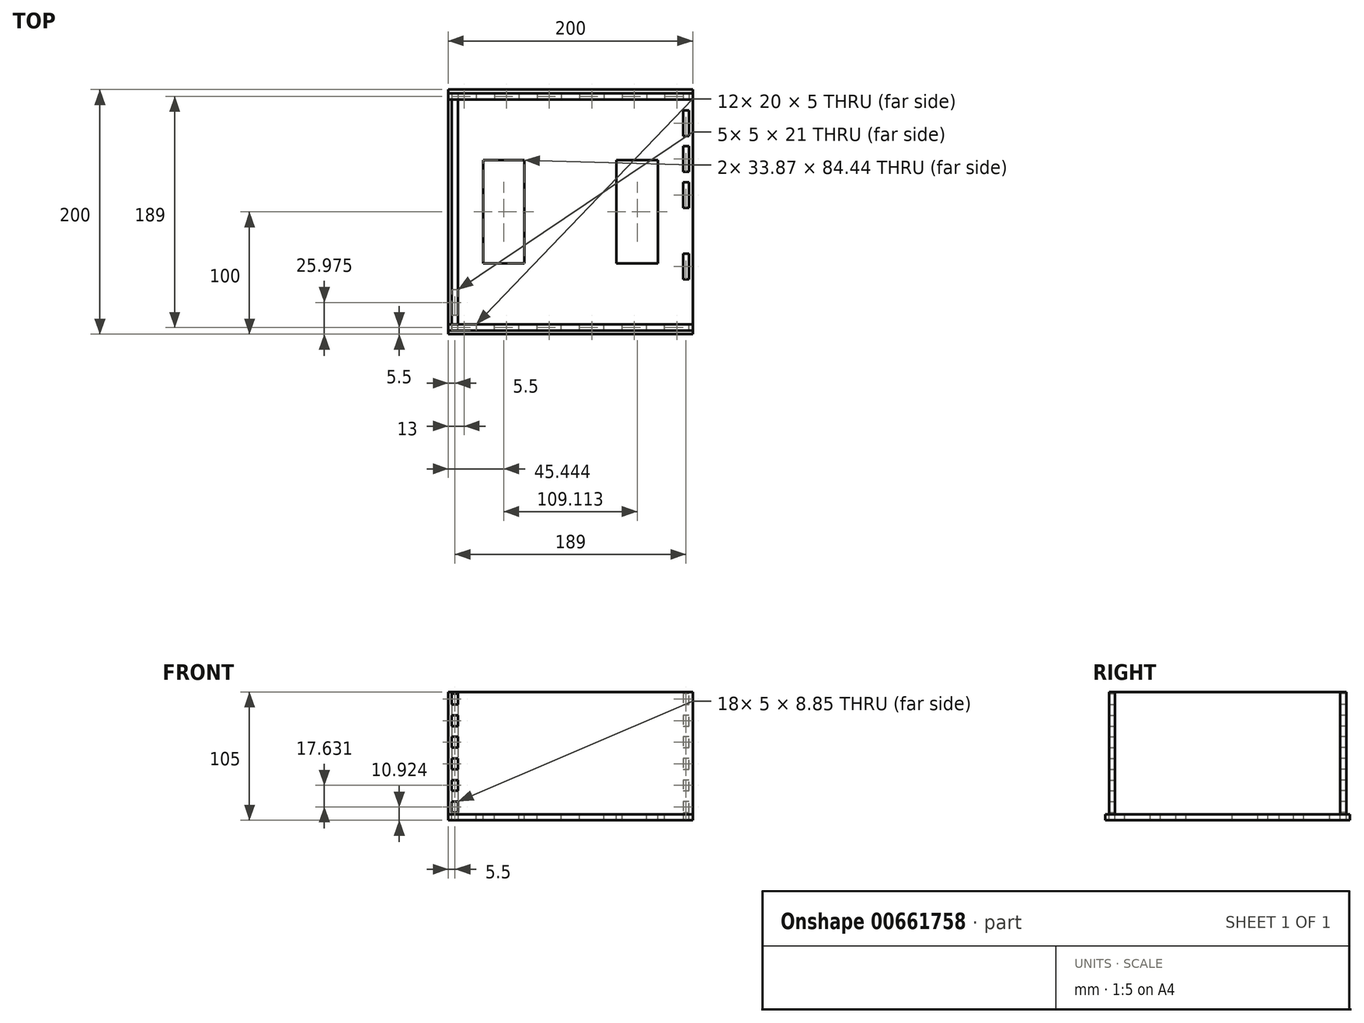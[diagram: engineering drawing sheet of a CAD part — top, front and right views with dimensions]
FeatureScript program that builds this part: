
annotation { "Feature Type Name" : "Feature", "Feature Type Description" : "" }
export const myFeature = defineFeature(function(context is Context, id is Id, definition is map)
    precondition{}
    {
        {
            assignVariable(context, id + "F0", {"name" : "width", "anyValue" : 5});
        }
        {
            var Q0;
            Q0=qCreatedBy(makeId("Top.planeOp"),FACE);
            var sketch = newSketch(context, id + "F1", { "sketchPlane" : qUnion([Q0])});
            skLineSegment(sketch, "E0.bottom", {"start": v(100, -100) * mm, "end": v(-100, -100) * mm});
            skLineSegment(sketch, "E0.top", {"start": v(100, 100) * mm, "end": v(-100, 100) * mm});
            skLineSegment(sketch, "E0.left", {"start": v(100, -100) * mm, "end": v(100, 100) * mm});
            skLineSegment(sketch, "E0.right", {"start": v(-100, -100) * mm, "end": v(-100, 100) * mm});
            skPoint(sketch, "E0.middle", {"position": v(0, 0) * mm});
            skLineSegment(sketch, "E1.0", {"start": v(97, 97) * mm, "end": v(-97, 97) * mm, "construction": true});
            skLineSegment(sketch, "E1.1", {"start": v(97, -97) * mm, "end": v(97, 97) * mm, "construction": true});
            skLineSegment(sketch, "E1.2", {"start": v(97, -97) * mm, "end": v(-97, -97) * mm, "construction": true});
            skLineSegment(sketch, "E1.3", {"start": v(-97, -97) * mm, "end": v(-97, 97) * mm, "construction": true});
            skSolve(sketch);
        }
        {
            var Q0;
            Q0=qSketchRegion(id+"F1",true);
            extrude(context, id + "F2", {"entities" : qUnion([Q0]), "depth" : (getVariable(context, 'width')) * mm});
        }
        {
            var Q0;
            Q0=makeQuery(id+"F2.opExtrude","CAP_FACE",FACE,{"disambiguationData":[OSD([sQuery(id+"F1.wireOp",EDGE,"E0.bottom"),sQuery(id+"F1.wireOp",EDGE,"E0.top"),sQuery(id+"F1.wireOp",EDGE,"E0.left"),sQuery(id+"F1.wireOp",EDGE,"E0.right")])],"isStart":false});
            var sketch = newSketch(context, id + "F3", { "sketchPlane" : qUnion([Q0])});
            skLineSegment(sketch, "E2.0", {"start": v(97, 97) * mm, "end": v(-97, 97) * mm, "construction": true});
            skLineSegment(sketch, "E2.1", {"start": v(97, -97) * mm, "end": v(97, 97) * mm, "construction": true});
            skLineSegment(sketch, "E2.2", {"start": v(97, -97) * mm, "end": v(-97, -97) * mm, "construction": true});
            skLineSegment(sketch, "E2.3", {"start": v(-97, -97) * mm, "end": v(-97, 97) * mm, "construction": true});
            skLineSegment(sketch, "E3.bottom", {"start": v(-97, 97) * mm, "end": v(-77, 97) * mm, "construction": true});
            skLineSegment(sketch, "E3.left", {"start": v(-97, 97) * mm, "end": v(-97, 92) * mm, "construction": true});
            skLineSegment(sketch, "E4.bottom", {"start": v(-97, 97) * mm, "end": v(-77, 97) * mm});
            skLineSegment(sketch, "E4.top", {"start": v(-97, 92) * mm, "end": v(-77, 92) * mm});
            skLineSegment(sketch, "E4.left", {"start": v(-97, 97) * mm, "end": v(-97, 92) * mm});
            skLineSegment(sketch, "E4.right", {"start": v(-77, 97) * mm, "end": v(-77, 92) * mm});
            skLineSegment(sketch, "E5.1.0.0", {"start": v(-42.2, 97) * mm, "end": v(-42.2, 92) * mm});
            skLineSegment(sketch, "E5.1.0.1", {"start": v(-62.2, 92) * mm, "end": v(-42.2, 92) * mm});
            skLineSegment(sketch, "E5.1.0.2", {"start": v(-62.2, 97) * mm, "end": v(-42.2, 97) * mm});
            skLineSegment(sketch, "E5.1.0.3", {"start": v(-62.2, 97) * mm, "end": v(-62.2, 92) * mm});
            skLineSegment(sketch, "E5.2.0.0", {"start": v(-7.4, 97) * mm, "end": v(-7.4, 92) * mm});
            skLineSegment(sketch, "E5.2.0.1", {"start": v(-27.4, 92) * mm, "end": v(-7.4, 92) * mm});
            skLineSegment(sketch, "E5.2.0.2", {"start": v(-27.4, 97) * mm, "end": v(-7.4, 97) * mm});
            skLineSegment(sketch, "E5.2.0.3", {"start": v(-27.4, 97) * mm, "end": v(-27.4, 92) * mm});
            skLineSegment(sketch, "E5.3.0.0", {"start": v(27.4, 97) * mm, "end": v(27.4, 92) * mm});
            skLineSegment(sketch, "E5.3.0.1", {"start": v(7.4, 92) * mm, "end": v(27.4, 92) * mm});
            skLineSegment(sketch, "E5.3.0.2", {"start": v(7.4, 97) * mm, "end": v(27.4, 97) * mm});
            skLineSegment(sketch, "E5.3.0.3", {"start": v(7.4, 97) * mm, "end": v(7.4, 92) * mm});
            skLineSegment(sketch, "E5.4.0.0", {"start": v(62.2, 97) * mm, "end": v(62.2, 92) * mm});
            skLineSegment(sketch, "E5.4.0.1", {"start": v(42.2, 92) * mm, "end": v(62.2, 92) * mm});
            skLineSegment(sketch, "E5.4.0.2", {"start": v(42.2, 97) * mm, "end": v(62.2, 97) * mm});
            skLineSegment(sketch, "E5.4.0.3", {"start": v(42.2, 97) * mm, "end": v(42.2, 92) * mm});
            skLineSegment(sketch, "E5.5.0.0", {"start": v(97, 97) * mm, "end": v(97, 92) * mm});
            skLineSegment(sketch, "E5.5.0.1", {"start": v(77, 92) * mm, "end": v(97, 92) * mm});
            skLineSegment(sketch, "E5.5.0.2", {"start": v(77, 97) * mm, "end": v(97, 97) * mm});
            skLineSegment(sketch, "E5.5.0.3", {"start": v(77, 97) * mm, "end": v(77, 92) * mm});
            skLineSegment(sketch, "E5.direction1", {"start": v(-77, 92) * mm, "end": v(-42.2, 92) * mm, "construction": true});
            skLineSegment(sketch, "E6.MirrorCS", {"start": v(-97, -97) * mm, "end": v(-97, -92) * mm});
            skLineSegment(sketch, "E7.MirrorCS", {"start": v(-77, -97) * mm, "end": v(-77, -92) * mm});
            skLineSegment(sketch, "E8.MirrorCS", {"start": v(-97, -97) * mm, "end": v(-97, -92) * mm, "construction": true});
            skLineSegment(sketch, "E9.MirrorCS", {"start": v(97, -97) * mm, "end": v(97, -92) * mm});
            skLineSegment(sketch, "E10.MirrorCS", {"start": v(77, -97) * mm, "end": v(77, -92) * mm});
            skLineSegment(sketch, "E11.MirrorCS", {"start": v(-42.2, -97) * mm, "end": v(-42.2, -92) * mm});
            skLineSegment(sketch, "E12.MirrorCS", {"start": v(62.2, -97) * mm, "end": v(62.2, -92) * mm});
            skLineSegment(sketch, "E13.MirrorCS", {"start": v(-62.2, -97) * mm, "end": v(-62.2, -92) * mm});
            skLineSegment(sketch, "E14.MirrorCS", {"start": v(-7.4, -97) * mm, "end": v(-7.4, -92) * mm});
            skLineSegment(sketch, "E15.MirrorCS", {"start": v(-27.4, -97) * mm, "end": v(-27.4, -92) * mm});
            skLineSegment(sketch, "E16.MirrorCS", {"start": v(7.4, -97) * mm, "end": v(7.4, -92) * mm});
            skLineSegment(sketch, "E17.MirrorCS", {"start": v(27.4, -97) * mm, "end": v(27.4, -92) * mm});
            skLineSegment(sketch, "E18.MirrorCS", {"start": v(42.2, -97) * mm, "end": v(42.2, -92) * mm});
            skLineSegment(sketch, "E19.MirrorCS", {"start": v(-62.2, -92) * mm, "end": v(-42.2, -92) * mm});
            skLineSegment(sketch, "E20.MirrorCS", {"start": v(-27.4, -97) * mm, "end": v(-7.4, -97) * mm});
            skLineSegment(sketch, "E21.MirrorCS", {"start": v(7.4, -97) * mm, "end": v(27.4, -97) * mm});
            skLineSegment(sketch, "E22.MirrorCS", {"start": v(42.2, -97) * mm, "end": v(62.2, -97) * mm});
            skLineSegment(sketch, "E23.MirrorCS", {"start": v(77, -97) * mm, "end": v(97, -97) * mm});
            skLineSegment(sketch, "E24.MirrorCS", {"start": v(-62.2, -97) * mm, "end": v(-42.2, -97) * mm});
            skLineSegment(sketch, "E25.MirrorCS", {"start": v(-97, -97) * mm, "end": v(-77, -97) * mm});
            skLineSegment(sketch, "E26.MirrorCS", {"start": v(42.2, -92) * mm, "end": v(62.2, -92) * mm});
            skLineSegment(sketch, "E27.MirrorCS", {"start": v(77, -92) * mm, "end": v(97, -92) * mm});
            skLineSegment(sketch, "E28.MirrorCS", {"start": v(-77, -92) * mm, "end": v(-42.2, -92) * mm, "construction": true});
            skLineSegment(sketch, "E29.MirrorCS", {"start": v(-27.4, -92) * mm, "end": v(-7.4, -92) * mm});
            skLineSegment(sketch, "E30.MirrorCS", {"start": v(-97, -97) * mm, "end": v(-77, -97) * mm, "construction": true});
            skLineSegment(sketch, "E31.MirrorCS", {"start": v(-97, -92) * mm, "end": v(-77, -92) * mm});
            skLineSegment(sketch, "E32.MirrorCS", {"start": v(7.4, -92) * mm, "end": v(27.4, -92) * mm});
            skSolve(sketch);
        }
        {
            var Q0;
            Q0=qSketchRegion(id+"F3",true);
            extrude(context, id + "F4", {"entities" : qUnion([Q0]), "operationType" : NewBodyOperationType.REMOVE, "oppositeDirection" : true, "depth" : 25 * mm});
        }
        {
            var Q0;
            Q0=makeQuery(id+"F2.opExtrude","CAP_FACE",FACE,{"disambiguationData":[OSD([sQuery(id+"F1.wireOp",EDGE,"E0.bottom"),sQuery(id+"F1.wireOp",EDGE,"E0.top"),sQuery(id+"F1.wireOp",EDGE,"E0.left"),sQuery(id+"F1.wireOp",EDGE,"E0.right")])],"isStart":false});
            var sketch = newSketch(context, id + "F5", { "sketchPlane" : qUnion([Q0])});
            skLineSegment(sketch, "E33.0", {"start": v(-97, 97) * mm, "end": v(-77, 97) * mm});
            skSolve(sketch);
        }
        {
            var Q0;
            Q0=makeQuery(id+"F5.imprint","IMPRINT",FACE,{"disambiguationData":[TD([[makeQuery(id+"F5.imprint","IMPRINT",EDGE,{"derivedFrom":makeQuery(id+"F4.boolean.opBoolean","COPY",EDGE,{"derivedFrom":makeQuery(id+"F4.opExtrude","CAP_EDGE",EDGE,{"disambiguationData":[OSD([sQuery(id+"F3.wireOp",EDGE,"E5.1.0.0")])],"isStart":true})})}),-1.0]])]});
            var Q1;
            Q1=makeQuery(id+"F5.imprint","IMPRINT",FACE,{"disambiguationData":[TD([[makeQuery(id+"F5.imprint","IMPRINT",EDGE,{"derivedFrom":sQuery(id+"F5.wireOp",EDGE,"E33.0")}),-1.0]])]});
            var Q2;
            Q2=makeQuery(id+"F5.imprint","IMPRINT",FACE,{"disambiguationData":[TD([[makeQuery(id+"F5.imprint","IMPRINT",EDGE,{"derivedFrom":makeQuery(id+"F4.boolean.opBoolean","COPY",EDGE,{"derivedFrom":makeQuery(id+"F4.opExtrude","CAP_EDGE",EDGE,{"disambiguationData":[OSD([sQuery(id+"F3.wireOp",EDGE,"E5.2.0.0")])],"isStart":true})})}),-1.0]])]});
            var Q3;
            Q3=makeQuery(id+"F5.imprint","IMPRINT",FACE,{"disambiguationData":[TD([[makeQuery(id+"F5.imprint","IMPRINT",EDGE,{"derivedFrom":makeQuery(id+"F4.boolean.opBoolean","COPY",EDGE,{"derivedFrom":makeQuery(id+"F4.opExtrude","CAP_EDGE",EDGE,{"disambiguationData":[OSD([sQuery(id+"F3.wireOp",EDGE,"E5.3.0.0")])],"isStart":true})})}),-1.0]])]});
            var Q4;
            Q4=makeQuery(id+"F5.imprint","IMPRINT",FACE,{"disambiguationData":[TD([[makeQuery(id+"F5.imprint","IMPRINT",EDGE,{"derivedFrom":makeQuery(id+"F4.boolean.opBoolean","COPY",EDGE,{"derivedFrom":makeQuery(id+"F4.opExtrude","CAP_EDGE",EDGE,{"disambiguationData":[OSD([sQuery(id+"F3.wireOp",EDGE,"E5.4.0.0")])],"isStart":true})})}),-1.0]])]});
            var Q5;
            Q5=makeQuery(id+"F5.imprint","IMPRINT",FACE,{"disambiguationData":[TD([[makeQuery(id+"F5.imprint","IMPRINT",EDGE,{"derivedFrom":makeQuery(id+"F4.boolean.opBoolean","COPY",EDGE,{"derivedFrom":makeQuery(id+"F4.opExtrude","CAP_EDGE",EDGE,{"disambiguationData":[OSD([sQuery(id+"F3.wireOp",EDGE,"E5.5.0.0")])],"isStart":true})})}),-1.0]])]});
            var Q6;
            Q6=makeQuery(id+"F2.opExtrude","CAP_FACE",FACE,{"disambiguationData":[OSD([sQuery(id+"F1.wireOp",EDGE,"E0.bottom"),sQuery(id+"F1.wireOp",EDGE,"E0.top"),sQuery(id+"F1.wireOp",EDGE,"E0.left"),sQuery(id+"F1.wireOp",EDGE,"E0.right")])],"isStart":true});
            extrude(context, id + "F6", {"entities" : qUnion([Q0, Q1, Q2, Q3, Q4, Q5]), "endBound" : BoundingType.UP_TO_SURFACE, "oppositeDirection" : true, "endBoundEntityFace" : qUnion([Q6]), "depth" : 25 * mm});
        }
        {
            var Q0;
            Q0=makeQuery(id+"F2.opExtrude","CAP_FACE",FACE,{"disambiguationData":[OSD([sQuery(id+"F1.wireOp",EDGE,"E0.bottom"),sQuery(id+"F1.wireOp",EDGE,"E0.top"),sQuery(id+"F1.wireOp",EDGE,"E0.left"),sQuery(id+"F1.wireOp",EDGE,"E0.right")])],"isStart":false});
            var sketch = newSketch(context, id + "F7", { "sketchPlane" : qUnion([Q0])});
            skLineSegment(sketch, "E34.bottom", {"start": v(-100, 97) * mm, "end": v(100, 97) * mm});
            skLineSegment(sketch, "E34.top", {"start": v(-100, 92) * mm, "end": v(100, 92) * mm});
            skLineSegment(sketch, "E34.left", {"start": v(-100, 97) * mm, "end": v(-100, 92) * mm});
            skLineSegment(sketch, "E34.right", {"start": v(100, 97) * mm, "end": v(100, 92) * mm});
            skSolve(sketch);
        }
        {
            var Q0;
            Q0=qSketchRegion(id+"F7",true);
            extrude(context, id + "F8", {"entities" : qUnion([Q0]), "depth" : 100 * mm});
        }
        {
            var Q0;
            Q0=makeQuery(id+"F2.opExtrude","CAP_FACE",FACE,{"disambiguationData":[OSD([sQuery(id+"F1.wireOp",EDGE,"E0.bottom"),sQuery(id+"F1.wireOp",EDGE,"E0.top"),sQuery(id+"F1.wireOp",EDGE,"E0.left"),sQuery(id+"F1.wireOp",EDGE,"E0.right")])],"isStart":true});
            var sketch = newSketch(context, id + "F9", { "sketchPlane" : qUnion([Q0])});
            skLineSegment(sketch, "E35.0", {"start": v(97, 97) * mm, "end": v(97, -97) * mm});
            skLineSegment(sketch, "E35.1", {"start": v(97, 97) * mm, "end": v(-97, 97) * mm});
            skLineSegment(sketch, "E35.2", {"start": v(-97, 97) * mm, "end": v(-97, -97) * mm});
            skLineSegment(sketch, "E35.3", {"start": v(97, -97) * mm, "end": v(-97, -97) * mm});
            skLineSegment(sketch, "E36.bottom", {"start": v(-97, 84.52) * mm, "end": v(-92, 84.52) * mm});
            skLineSegment(sketch, "E36.top", {"start": v(-97, 63.52) * mm, "end": v(-92, 63.52) * mm});
            skLineSegment(sketch, "E36.left", {"start": v(-97, 84.52) * mm, "end": v(-97, 63.52) * mm});
            skLineSegment(sketch, "E36.right", {"start": v(-92, 84.52) * mm, "end": v(-92, 63.52) * mm});
            skLineSegment(sketch, "E37.1.0.0", {"start": v(-97, 55.22) * mm, "end": v(-97, 34.22) * mm});
            skLineSegment(sketch, "E37.1.0.1", {"start": v(-97, 55.22) * mm, "end": v(-92, 55.22) * mm});
            skLineSegment(sketch, "E37.1.0.2", {"start": v(-97, 34.22) * mm, "end": v(-92, 34.22) * mm});
            skLineSegment(sketch, "E37.1.0.3", {"start": v(-92, 55.22) * mm, "end": v(-92, 34.22) * mm});
            skLineSegment(sketch, "E37.2.0.0", {"start": v(-97, 25.91) * mm, "end": v(-97, 4.91) * mm});
            skLineSegment(sketch, "E37.2.0.1", {"start": v(-97, 25.91) * mm, "end": v(-92, 25.91) * mm});
            skLineSegment(sketch, "E37.2.0.2", {"start": v(-97, 4.91) * mm, "end": v(-92, 4.91) * mm});
            skLineSegment(sketch, "E37.2.0.3", {"start": v(-92, 25.91) * mm, "end": v(-92, 4.91) * mm});
            skLineSegment(sketch, "E37.3.0.0", {"start": v(-97, -3.4) * mm, "end": v(-97, -24.4) * mm});
            skLineSegment(sketch, "E37.3.0.1", {"start": v(-97, -3.4) * mm, "end": v(-92, -3.4) * mm});
            skLineSegment(sketch, "E37.3.0.2", {"start": v(-97, -24.4) * mm, "end": v(-92, -24.4) * mm});
            skLineSegment(sketch, "E37.3.0.3", {"start": v(-92, -3.4) * mm, "end": v(-92, -24.4) * mm});
            skLineSegment(sketch, "E37.4.0.0", {"start": v(-97, -32.7) * mm, "end": v(-97, -53.7) * mm});
            skLineSegment(sketch, "E37.4.0.1", {"start": v(-97, -32.7) * mm, "end": v(-92, -32.7) * mm});
            skLineSegment(sketch, "E37.4.0.2", {"start": v(-97, -53.7) * mm, "end": v(-92, -53.7) * mm});
            skLineSegment(sketch, "E37.4.0.3", {"start": v(-92, -32.7) * mm, "end": v(-92, -53.7) * mm});
            skLineSegment(sketch, "E37.5.0.0", {"start": v(-97, -62) * mm, "end": v(-97, -83) * mm});
            skLineSegment(sketch, "E37.5.0.1", {"start": v(-97, -62) * mm, "end": v(-92, -62) * mm});
            skLineSegment(sketch, "E37.5.0.2", {"start": v(-97, -83) * mm, "end": v(-92, -83) * mm});
            skLineSegment(sketch, "E37.5.0.3", {"start": v(-92, -62) * mm, "end": v(-92, -83) * mm});
            skLineSegment(sketch, "E37.direction1", {"start": v(-97, 63.52) * mm, "end": v(-97, 34.22) * mm, "construction": true});
            skLineSegment(sketch, "E38.MirrorCS", {"start": v(97, 84.52) * mm, "end": v(97, 63.52) * mm});
            skLineSegment(sketch, "E39.MirrorCS", {"start": v(97, 84.52) * mm, "end": v(92, 84.52) * mm});
            skLineSegment(sketch, "E40.MirrorCS", {"start": v(92, 84.52) * mm, "end": v(92, 63.52) * mm});
            skLineSegment(sketch, "E41.MirrorCS", {"start": v(97, 63.52) * mm, "end": v(92, 63.52) * mm});
            skLineSegment(sketch, "E42.MirrorCS", {"start": v(97, 55.22) * mm, "end": v(92, 55.22) * mm});
            skLineSegment(sketch, "E43.MirrorCS", {"start": v(92, 55.22) * mm, "end": v(92, 34.22) * mm});
            skLineSegment(sketch, "E44.MirrorCS", {"start": v(97, 63.52) * mm, "end": v(97, 34.22) * mm, "construction": true});
            skLineSegment(sketch, "E45.MirrorCS", {"start": v(97, 55.22) * mm, "end": v(97, 34.22) * mm});
            skLineSegment(sketch, "E46.MirrorCS", {"start": v(97, 25.91) * mm, "end": v(97, 4.91) * mm});
            skLineSegment(sketch, "E47.MirrorCS", {"start": v(97, 34.22) * mm, "end": v(92, 34.22) * mm});
            skLineSegment(sketch, "E48.MirrorCS", {"start": v(97, 25.91) * mm, "end": v(92, 25.91) * mm});
            skLineSegment(sketch, "E49.MirrorCS", {"start": v(92, 25.91) * mm, "end": v(92, 4.91) * mm});
            skLineSegment(sketch, "E50.MirrorCS", {"start": v(97, 4.91) * mm, "end": v(92, 4.91) * mm});
            skLineSegment(sketch, "E51.MirrorCS", {"start": v(97, -32.7) * mm, "end": v(92, -32.7) * mm});
            skLineSegment(sketch, "E52.MirrorCS", {"start": v(92, -32.7) * mm, "end": v(92, -53.7) * mm});
            skLineSegment(sketch, "E53.MirrorCS", {"start": v(97, -32.7) * mm, "end": v(97, -53.7) * mm});
            skLineSegment(sketch, "E54.MirrorCS", {"start": v(97, -53.7) * mm, "end": v(92, -53.7) * mm});
            skLineSegment(sketch, "E55.MirrorCS", {"start": v(97, -62) * mm, "end": v(92, -62) * mm});
            skLineSegment(sketch, "E56.MirrorCS", {"start": v(92, -62) * mm, "end": v(92, -83) * mm});
            skLineSegment(sketch, "E57.MirrorCS", {"start": v(97, -62) * mm, "end": v(97, -83) * mm});
            skLineSegment(sketch, "E58.MirrorCS", {"start": v(97, -83) * mm, "end": v(92, -83) * mm});
            skLineSegment(sketch, "E59.MirrorCS", {"start": v(92, -3.4) * mm, "end": v(92, -24.4) * mm});
            skLineSegment(sketch, "E60.MirrorCS", {"start": v(97, -3.4) * mm, "end": v(92, -3.4) * mm});
            skLineSegment(sketch, "E61.MirrorCS", {"start": v(97, -24.4) * mm, "end": v(92, -24.4) * mm});
            skLineSegment(sketch, "E62.MirrorCS", {"start": v(97, -3.4) * mm, "end": v(97, -24.4) * mm});
            skSolve(sketch);
        }
        {
            var Q0;
            Q0=makeQuery(id+"F9.imprint","IMPRINT",FACE,{"disambiguationData":[TD([[makeQuery(id+"F9.imprint","IMPRINT",EDGE,{"derivedFrom":sQuery(id+"F9.wireOp",EDGE,"E38.MirrorCS")}),-1.0]])]});
            var Q1;
            Q1=makeQuery(id+"F9.imprint","IMPRINT",FACE,{"disambiguationData":[TD([[makeQuery(id+"F9.imprint","IMPRINT",EDGE,{"derivedFrom":sQuery(id+"F9.wireOp",EDGE,"E42.MirrorCS")}),1.0]])]});
            var Q2;
            Q2=makeQuery(id+"F9.imprint","IMPRINT",FACE,{"disambiguationData":[TD([[makeQuery(id+"F9.imprint","IMPRINT",EDGE,{"derivedFrom":sQuery(id+"F9.wireOp",EDGE,"E46.MirrorCS")}),-1.0]])]});
            var Q3;
            Q3=makeQuery(id+"F9.imprint","IMPRINT",FACE,{"disambiguationData":[TD([[makeQuery(id+"F9.imprint","IMPRINT",EDGE,{"derivedFrom":sQuery(id+"F9.wireOp",EDGE,"E59.MirrorCS")}),1.0]])]});
            var Q4;
            Q4=makeQuery(id+"F9.imprint","IMPRINT",FACE,{"disambiguationData":[TD([[makeQuery(id+"F9.imprint","IMPRINT",EDGE,{"derivedFrom":sQuery(id+"F9.wireOp",EDGE,"E51.MirrorCS")}),1.0]])]});
            var Q5;
            Q5=makeQuery(id+"F9.imprint","IMPRINT",FACE,{"disambiguationData":[TD([[makeQuery(id+"F9.imprint","IMPRINT",EDGE,{"derivedFrom":sQuery(id+"F9.wireOp",EDGE,"E55.MirrorCS")}),1.0]])]});
            var Q6;
            Q6=makeQuery(id+"F9.imprint","IMPRINT",FACE,{"disambiguationData":[TD([[makeQuery(id+"F9.imprint","IMPRINT",EDGE,{"derivedFrom":sQuery(id+"F9.wireOp",EDGE,"E36.bottom")}),-1.0]])]});
            var Q7;
            Q7=makeQuery(id+"F9.imprint","IMPRINT",FACE,{"disambiguationData":[TD([[makeQuery(id+"F9.imprint","IMPRINT",EDGE,{"derivedFrom":sQuery(id+"F9.wireOp",EDGE,"E37.1.0.0")}),1.0]])]});
            var Q8;
            Q8=makeQuery(id+"F9.imprint","IMPRINT",FACE,{"disambiguationData":[TD([[makeQuery(id+"F9.imprint","IMPRINT",EDGE,{"derivedFrom":sQuery(id+"F9.wireOp",EDGE,"E37.2.0.0")}),1.0]])]});
            var Q9;
            Q9=makeQuery(id+"F9.imprint","IMPRINT",FACE,{"disambiguationData":[TD([[makeQuery(id+"F9.imprint","IMPRINT",EDGE,{"derivedFrom":sQuery(id+"F9.wireOp",EDGE,"E37.3.0.0")}),1.0]])]});
            var Q10;
            Q10=makeQuery(id+"F9.imprint","IMPRINT",FACE,{"disambiguationData":[TD([[makeQuery(id+"F9.imprint","IMPRINT",EDGE,{"derivedFrom":sQuery(id+"F9.wireOp",EDGE,"E37.4.0.0")}),1.0]])]});
            var Q11;
            Q11=makeQuery(id+"F9.imprint","IMPRINT",FACE,{"disambiguationData":[TD([[makeQuery(id+"F9.imprint","IMPRINT",EDGE,{"derivedFrom":sQuery(id+"F9.wireOp",EDGE,"E37.5.0.0")}),1.0]])]});
            extrude(context, id + "F10", {"entities" : qUnion([Q0, Q1, Q2, Q3, Q4, Q5, Q6, Q7, Q8, Q9, Q10, Q11]), "operationType" : NewBodyOperationType.REMOVE, "oppositeDirection" : true, "depth" : 25 * mm});
        }
        {
            var Q0;
            Q0=makeQuery(id+"F8.opExtrude","SWEPT_BODY",BODY,{"disambiguationData":[OSD([sQuery(id+"F7.wireOp",EDGE,"E34.bottom"),sQuery(id+"F7.wireOp",EDGE,"E34.top"),sQuery(id+"F7.wireOp",EDGE,"E34.left"),sQuery(id+"F7.wireOp",EDGE,"E34.right")])]});
            var Q1;
            Q1=makeQuery(id+"F6.opExtrude","SWEPT_BODY",BODY,{"disambiguationData":[OSD([sQuery(id+"F3.wireOp",EDGE,"E5.5.0.0"),sQuery(id+"F3.wireOp",EDGE,"E5.5.0.1"),sQuery(id+"F3.wireOp",EDGE,"E5.5.0.2"),sQuery(id+"F3.wireOp",EDGE,"E5.5.0.3")])]});
            var Q2;
            Q2=makeQuery(id+"F6.opExtrude","SWEPT_BODY",BODY,{"disambiguationData":[OSD([sQuery(id+"F3.wireOp",EDGE,"E5.4.0.0"),sQuery(id+"F3.wireOp",EDGE,"E5.4.0.1"),sQuery(id+"F3.wireOp",EDGE,"E5.4.0.2"),sQuery(id+"F3.wireOp",EDGE,"E5.4.0.3")])]});
            var Q3;
            Q3=makeQuery(id+"F6.opExtrude","SWEPT_BODY",BODY,{"disambiguationData":[OSD([sQuery(id+"F3.wireOp",EDGE,"E5.3.0.0"),sQuery(id+"F3.wireOp",EDGE,"E5.3.0.1"),sQuery(id+"F3.wireOp",EDGE,"E5.3.0.2"),sQuery(id+"F3.wireOp",EDGE,"E5.3.0.3")])]});
            var Q4;
            Q4=makeQuery(id+"F6.opExtrude","SWEPT_BODY",BODY,{"disambiguationData":[OSD([sQuery(id+"F3.wireOp",EDGE,"E5.2.0.0"),sQuery(id+"F3.wireOp",EDGE,"E5.2.0.1"),sQuery(id+"F3.wireOp",EDGE,"E5.2.0.2"),sQuery(id+"F3.wireOp",EDGE,"E5.2.0.3")])]});
            var Q5;
            Q5=makeQuery(id+"F6.opExtrude","SWEPT_BODY",BODY,{"disambiguationData":[OSD([sQuery(id+"F3.wireOp",EDGE,"E5.1.0.0"),sQuery(id+"F3.wireOp",EDGE,"E5.1.0.1"),sQuery(id+"F3.wireOp",EDGE,"E5.1.0.2"),sQuery(id+"F3.wireOp",EDGE,"E5.1.0.3")])]});
            var Q6;
            Q6=makeQuery(id+"F6.opExtrude","SWEPT_BODY",BODY,{"disambiguationData":[OSD([sQuery(id+"F3.wireOp",EDGE,"E4.top"),sQuery(id+"F3.wireOp",EDGE,"E4.left"),sQuery(id+"F3.wireOp",EDGE,"E4.right"),sQuery(id+"F5.wireOp",EDGE,"E33.0")])]});
            booleanBodies(context, id + "F11", {"operationType" : BooleanOperationType.UNION, "tools" : qUnion([Q0, Q1, Q2, Q3, Q4, Q5, Q6])});
        }
        {
            var Q0;
            Q0=makeQuery(id+"F11.opBoolean","MERGE",FACE,{"derivedFrom":[makeQuery(id+"F6.opExtrude","SWEPT_FACE",FACE,{"disambiguationData":[OSD([sQuery(id+"F3.wireOp",EDGE,"E4.top")])]}),makeQuery(id+"F6.opExtrude","SWEPT_FACE",FACE,{"disambiguationData":[OSD([sQuery(id+"F3.wireOp",EDGE,"E5.1.0.1")])]}),makeQuery(id+"F6.opExtrude","SWEPT_FACE",FACE,{"disambiguationData":[OSD([sQuery(id+"F3.wireOp",EDGE,"E5.2.0.1")])]}),makeQuery(id+"F6.opExtrude","SWEPT_FACE",FACE,{"disambiguationData":[OSD([sQuery(id+"F3.wireOp",EDGE,"E5.3.0.1")])]}),makeQuery(id+"F6.opExtrude","SWEPT_FACE",FACE,{"disambiguationData":[OSD([sQuery(id+"F3.wireOp",EDGE,"E5.4.0.1")])]}),makeQuery(id+"F6.opExtrude","SWEPT_FACE",FACE,{"disambiguationData":[OSD([sQuery(id+"F3.wireOp",EDGE,"E5.5.0.1")])]}),makeQuery(id+"F8.opExtrude","SWEPT_FACE",FACE,{"disambiguationData":[OSD([sQuery(id+"F7.wireOp",EDGE,"E34.top")])]})]});
            var sketch = newSketch(context, id + "F12", { "sketchPlane" : qUnion([Q0])});
            skLineSegment(sketch, "E63.bottom", {"start": v(-100, 105) * mm, "end": v(100, 105) * mm});
            skLineSegment(sketch, "E63.top", {"start": v(-100, 5) * mm, "end": v(100, 5) * mm});
            skLineSegment(sketch, "E63.left", {"start": v(-100, 105) * mm, "end": v(-100, 5) * mm});
            skLineSegment(sketch, "E63.right", {"start": v(100, 105) * mm, "end": v(100, 5) * mm});
            skLineSegment(sketch, "E64.bottom", {"start": v(-147, 8) * mm, "end": v(-142, 8) * mm});
            skLineSegment(sketch, "E64.top", {"start": v(-147, 18) * mm, "end": v(-142, 18) * mm});
            skLineSegment(sketch, "E64.left", {"start": v(-147, 8) * mm, "end": v(-147, 18) * mm});
            skLineSegment(sketch, "E64.right", {"start": v(-142, 8) * mm, "end": v(-142, 18) * mm});
            skLineSegment(sketch, "E65.1.0.0", {"start": v(-142, 24.8) * mm, "end": v(-142, 34.8) * mm});
            skLineSegment(sketch, "E65.1.0.1", {"start": v(-147, 34.8) * mm, "end": v(-142, 34.8) * mm});
            skLineSegment(sketch, "E65.1.0.2", {"start": v(-147, 24.8) * mm, "end": v(-147, 34.8) * mm});
            skLineSegment(sketch, "E65.1.0.3", {"start": v(-147, 24.8) * mm, "end": v(-142, 24.8) * mm});
            skLineSegment(sketch, "E65.2.0.0", {"start": v(-142, 41.6) * mm, "end": v(-142, 51.6) * mm});
            skLineSegment(sketch, "E65.2.0.1", {"start": v(-147, 51.6) * mm, "end": v(-142, 51.6) * mm});
            skLineSegment(sketch, "E65.2.0.2", {"start": v(-147, 41.6) * mm, "end": v(-147, 51.6) * mm});
            skLineSegment(sketch, "E65.2.0.3", {"start": v(-147, 41.6) * mm, "end": v(-142, 41.6) * mm});
            skLineSegment(sketch, "E65.3.0.0", {"start": v(-142, 58.4) * mm, "end": v(-142, 68.4) * mm});
            skLineSegment(sketch, "E65.3.0.1", {"start": v(-147, 68.4) * mm, "end": v(-142, 68.4) * mm});
            skLineSegment(sketch, "E65.3.0.2", {"start": v(-147, 58.4) * mm, "end": v(-147, 68.4) * mm});
            skLineSegment(sketch, "E65.3.0.3", {"start": v(-147, 58.4) * mm, "end": v(-142, 58.4) * mm});
            skLineSegment(sketch, "E65.4.0.0", {"start": v(-142, 75.2) * mm, "end": v(-142, 85.2) * mm});
            skLineSegment(sketch, "E65.4.0.1", {"start": v(-147, 85.2) * mm, "end": v(-142, 85.2) * mm});
            skLineSegment(sketch, "E65.4.0.2", {"start": v(-147, 75.2) * mm, "end": v(-147, 85.2) * mm});
            skLineSegment(sketch, "E65.4.0.3", {"start": v(-147, 75.2) * mm, "end": v(-142, 75.2) * mm});
            skLineSegment(sketch, "E65.5.0.0", {"start": v(-142, 92) * mm, "end": v(-142, 102) * mm});
            skLineSegment(sketch, "E65.5.0.1", {"start": v(-147, 102) * mm, "end": v(-142, 102) * mm});
            skLineSegment(sketch, "E65.5.0.2", {"start": v(-147, 92) * mm, "end": v(-147, 102) * mm});
            skLineSegment(sketch, "E65.5.0.3", {"start": v(-147, 92) * mm, "end": v(-142, 92) * mm});
            skLineSegment(sketch, "E65.direction1", {"start": v(-142, 8) * mm, "end": v(-142, 24.8) * mm, "construction": true});
            skLineSegment(sketch, "E66.MirrorCS", {"start": v(142, 92) * mm, "end": v(142, 102) * mm});
            skLineSegment(sketch, "E67.MirrorCS", {"start": v(147, 102) * mm, "end": v(142, 102) * mm});
            skLineSegment(sketch, "E68.MirrorCS", {"start": v(147, 92) * mm, "end": v(147, 102) * mm});
            skLineSegment(sketch, "E69.MirrorCS", {"start": v(147, 92) * mm, "end": v(142, 92) * mm});
            skLineSegment(sketch, "E70.MirrorCS", {"start": v(147, 51.6) * mm, "end": v(142, 51.6) * mm});
            skLineSegment(sketch, "E71.MirrorCS", {"start": v(147, 58.4) * mm, "end": v(142, 58.4) * mm});
            skLineSegment(sketch, "E72.MirrorCS", {"start": v(147, 75.2) * mm, "end": v(142, 75.2) * mm});
            skLineSegment(sketch, "E73.MirrorCS", {"start": v(147, 41.6) * mm, "end": v(142, 41.6) * mm});
            skLineSegment(sketch, "E74.MirrorCS", {"start": v(147, 18) * mm, "end": v(142, 18) * mm});
            skLineSegment(sketch, "E75.MirrorCS", {"start": v(147, 68.4) * mm, "end": v(142, 68.4) * mm});
            skLineSegment(sketch, "E76.MirrorCS", {"start": v(147, 85.2) * mm, "end": v(142, 85.2) * mm});
            skLineSegment(sketch, "E77.MirrorCS", {"start": v(147, 24.8) * mm, "end": v(142, 24.8) * mm});
            skLineSegment(sketch, "E78.MirrorCS", {"start": v(142, 75.2) * mm, "end": v(142, 85.2) * mm});
            skLineSegment(sketch, "E79.MirrorCS", {"start": v(147, 41.6) * mm, "end": v(147, 51.6) * mm});
            skLineSegment(sketch, "E80.MirrorCS", {"start": v(100, 5) * mm, "end": v(-100, 5) * mm});
            skLineSegment(sketch, "E81.MirrorCS", {"start": v(147, 8) * mm, "end": v(142, 8) * mm});
            skLineSegment(sketch, "E82.MirrorCS", {"start": v(147, 8) * mm, "end": v(147, 18) * mm});
            skLineSegment(sketch, "E83.MirrorCS", {"start": v(142, 8) * mm, "end": v(142, 24.8) * mm, "construction": true});
            skLineSegment(sketch, "E84.MirrorCS", {"start": v(142, 24.8) * mm, "end": v(142, 34.8) * mm});
            skLineSegment(sketch, "E85.MirrorCS", {"start": v(147, 34.8) * mm, "end": v(142, 34.8) * mm});
            skLineSegment(sketch, "E86.MirrorCS", {"start": v(147, 24.8) * mm, "end": v(147, 34.8) * mm});
            skLineSegment(sketch, "E87.MirrorCS", {"start": v(142, 41.6) * mm, "end": v(142, 51.6) * mm});
            skLineSegment(sketch, "E88.MirrorCS", {"start": v(142, 58.4) * mm, "end": v(142, 68.4) * mm});
            skLineSegment(sketch, "E89.MirrorCS", {"start": v(147, 58.4) * mm, "end": v(147, 68.4) * mm});
            skLineSegment(sketch, "E90.MirrorCS", {"start": v(147, 75.2) * mm, "end": v(147, 85.2) * mm});
            skLineSegment(sketch, "E91", {"start": v(142, 18) * mm, "end": v(142, 8) * mm});
            skSolve(sketch);
        }
        {
            var Q0;
            Q0=makeQuery(id+"F12.imprint","IMPRINT",FACE,{"disambiguationData":[TD([[makeQuery(id+"F12.imprint","IMPRINT",EDGE,{"derivedFrom":sQuery(id+"F12.wireOp",EDGE,"E65.5.0.0")}),1.0]])]});
            var Q1;
            Q1=makeQuery(id+"F12.imprint","IMPRINT",FACE,{"disambiguationData":[TD([[makeQuery(id+"F12.imprint","IMPRINT",EDGE,{"derivedFrom":sQuery(id+"F12.wireOp",EDGE,"E65.4.0.0")}),1.0]])]});
            var Q2;
            Q2=makeQuery(id+"F12.imprint","IMPRINT",FACE,{"disambiguationData":[TD([[makeQuery(id+"F12.imprint","IMPRINT",EDGE,{"derivedFrom":sQuery(id+"F12.wireOp",EDGE,"E65.3.0.0")}),1.0]])]});
            var Q3;
            Q3=makeQuery(id+"F12.imprint","IMPRINT",FACE,{"disambiguationData":[TD([[makeQuery(id+"F12.imprint","IMPRINT",EDGE,{"derivedFrom":sQuery(id+"F12.wireOp",EDGE,"E65.2.0.0")}),1.0]])]});
            var Q4;
            Q4=makeQuery(id+"F12.imprint","IMPRINT",FACE,{"disambiguationData":[TD([[makeQuery(id+"F12.imprint","IMPRINT",EDGE,{"derivedFrom":sQuery(id+"F12.wireOp",EDGE,"E65.1.0.0")}),1.0]])]});
            var Q5;
            Q5=makeQuery(id+"F12.imprint","IMPRINT",FACE,{"disambiguationData":[TD([[makeQuery(id+"F12.imprint","IMPRINT",EDGE,{"derivedFrom":sQuery(id+"F12.wireOp",EDGE,"E64.bottom")}),1.0]])]});
            var Q6;
            Q6=makeQuery(id+"F12.imprint","IMPRINT",FACE,{"disambiguationData":[TD([[makeQuery(id+"F12.imprint","IMPRINT",EDGE,{"derivedFrom":sQuery(id+"F12.wireOp",EDGE,"E66.MirrorCS")}),-1.0]])]});
            var Q7;
            Q7=makeQuery(id+"F12.imprint","IMPRINT",FACE,{"disambiguationData":[TD([[makeQuery(id+"F12.imprint","IMPRINT",EDGE,{"derivedFrom":sQuery(id+"F12.wireOp",EDGE,"E72.MirrorCS")}),-1.0]])]});
            var Q8;
            Q8=makeQuery(id+"F12.imprint","IMPRINT",FACE,{"disambiguationData":[TD([[makeQuery(id+"F12.imprint","IMPRINT",EDGE,{"derivedFrom":sQuery(id+"F12.wireOp",EDGE,"E71.MirrorCS")}),-1.0]])]});
            var Q9;
            Q9=makeQuery(id+"F12.imprint","IMPRINT",FACE,{"disambiguationData":[TD([[makeQuery(id+"F12.imprint","IMPRINT",EDGE,{"derivedFrom":sQuery(id+"F12.wireOp",EDGE,"E70.MirrorCS")}),1.0]])]});
            var Q10;
            Q10=makeQuery(id+"F12.imprint","IMPRINT",FACE,{"disambiguationData":[TD([[makeQuery(id+"F12.imprint","IMPRINT",EDGE,{"derivedFrom":sQuery(id+"F12.wireOp",EDGE,"E77.MirrorCS")}),-1.0]])]});
            var Q11;
            Q11=makeQuery(id+"F12.imprint","IMPRINT",FACE,{"disambiguationData":[TD([[makeQuery(id+"F12.imprint","IMPRINT",EDGE,{"derivedFrom":sQuery(id+"F12.wireOp",EDGE,"E82.MirrorCS")}),1.0]])]});
            extrude(context, id + "F13", {"entities" : qUnion([Q0, Q1, Q2, Q3, Q4, Q5, Q6, Q7, Q8, Q9, Q10, Q11]), "operationType" : NewBodyOperationType.REMOVE, "oppositeDirection" : true, "depth" : 25 * mm});
        }
        {
            var Q0;
            Q0=makeQuery(id+"F2.opExtrude","CAP_FACE",FACE,{"disambiguationData":[OSD([sQuery(id+"F1.wireOp",EDGE,"E0.bottom"),sQuery(id+"F1.wireOp",EDGE,"E0.top"),sQuery(id+"F1.wireOp",EDGE,"E0.left"),sQuery(id+"F1.wireOp",EDGE,"E0.right")])],"isStart":false});
            var sketch = newSketch(context, id + "F14", { "sketchPlane" : qUnion([Q0])});
            skLineSegment(sketch, "E92.bottom", {"start": v(-97, 92) * mm, "end": v(-92, 92) * mm});
            skLineSegment(sketch, "E92.top", {"start": v(-97, -92) * mm, "end": v(-92, -92) * mm});
            skLineSegment(sketch, "E92.left", {"start": v(-97, 92) * mm, "end": v(-97, -92) * mm});
            skLineSegment(sketch, "E92.right", {"start": v(-92, 92) * mm, "end": v(-92, -92) * mm});
            skSolve(sketch);
        }
        {
            var Q0;
            Q0=qSketchRegion(id+"F14",true);
            extrude(context, id + "F15", {"entities" : qUnion([Q0]), "depth" : 100 * mm});
        }
        {
            var Q0;
            Q0=makeQuery(id+"F9.imprint","IMPRINT",FACE,{"disambiguationData":[TD([[makeQuery(id+"F9.imprint","IMPRINT",EDGE,{"derivedFrom":sQuery(id+"F9.wireOp",EDGE,"E36.bottom")}),-1.0]])]});
            var Q1;
            Q1=makeQuery(id+"F9.imprint","IMPRINT",FACE,{"disambiguationData":[TD([[makeQuery(id+"F9.imprint","IMPRINT",EDGE,{"derivedFrom":sQuery(id+"F9.wireOp",EDGE,"E37.1.0.0")}),1.0]])]});
            var Q2;
            Q2=makeQuery(id+"F9.imprint","IMPRINT",FACE,{"disambiguationData":[TD([[makeQuery(id+"F9.imprint","IMPRINT",EDGE,{"derivedFrom":sQuery(id+"F9.wireOp",EDGE,"E37.2.0.0")}),1.0]])]});
            var Q3;
            Q3=makeQuery(id+"F9.imprint","IMPRINT",FACE,{"disambiguationData":[TD([[makeQuery(id+"F9.imprint","IMPRINT",EDGE,{"derivedFrom":sQuery(id+"F9.wireOp",EDGE,"E37.3.0.0")}),1.0]])]});
            var Q4;
            Q4=makeQuery(id+"F9.imprint","IMPRINT",FACE,{"disambiguationData":[TD([[makeQuery(id+"F9.imprint","IMPRINT",EDGE,{"derivedFrom":sQuery(id+"F9.wireOp",EDGE,"E37.4.0.0")}),1.0]])]});
            var Q5;
            Q5=makeQuery(id+"F9.imprint","IMPRINT",FACE,{"disambiguationData":[TD([[makeQuery(id+"F9.imprint","IMPRINT",EDGE,{"derivedFrom":sQuery(id+"F9.wireOp",EDGE,"E37.5.0.0")}),1.0]])]});
            var Q6;
            Q6=makeQuery(id+"F2.opExtrude","CAP_FACE",FACE,{"disambiguationData":[OSD([sQuery(id+"F1.wireOp",EDGE,"E0.bottom"),sQuery(id+"F1.wireOp",EDGE,"E0.top"),sQuery(id+"F1.wireOp",EDGE,"E0.left"),sQuery(id+"F1.wireOp",EDGE,"E0.right")])],"isStart":false});
            extrude(context, id + "F16", {"entities" : qUnion([Q0, Q1, Q2, Q3, Q4, Q5]), "endBound" : BoundingType.UP_TO_SURFACE, "oppositeDirection" : true, "endBoundEntityFace" : qUnion([Q6]), "depth" : 25 * mm});
        }
        {
            var Q0;
            Q0=makeQuery(id+"F15.opExtrude","SWEPT_BODY",BODY,{"disambiguationData":[OSD([sQuery(id+"F14.wireOp",EDGE,"E92.bottom"),sQuery(id+"F14.wireOp",EDGE,"E92.top"),sQuery(id+"F14.wireOp",EDGE,"E92.left"),sQuery(id+"F14.wireOp",EDGE,"E92.right")])]});
            var Q1;
            Q1=makeQuery(id+"F16.opExtrude","SWEPT_BODY",BODY,{"disambiguationData":[OSD([sQuery(id+"F9.wireOp",EDGE,"E37.5.0.0"),sQuery(id+"F9.wireOp",EDGE,"E37.5.0.1"),sQuery(id+"F9.wireOp",EDGE,"E37.5.0.2"),sQuery(id+"F9.wireOp",EDGE,"E37.5.0.3")])]});
            var Q2;
            Q2=makeQuery(id+"F16.opExtrude","SWEPT_BODY",BODY,{"disambiguationData":[OSD([sQuery(id+"F9.wireOp",EDGE,"E37.4.0.0"),sQuery(id+"F9.wireOp",EDGE,"E37.4.0.1"),sQuery(id+"F9.wireOp",EDGE,"E37.4.0.2"),sQuery(id+"F9.wireOp",EDGE,"E37.4.0.3")])]});
            var Q3;
            Q3=makeQuery(id+"F16.opExtrude","SWEPT_BODY",BODY,{"disambiguationData":[OSD([sQuery(id+"F9.wireOp",EDGE,"E37.3.0.0"),sQuery(id+"F9.wireOp",EDGE,"E37.3.0.1"),sQuery(id+"F9.wireOp",EDGE,"E37.3.0.2"),sQuery(id+"F9.wireOp",EDGE,"E37.3.0.3")])]});
            var Q4;
            Q4=makeQuery(id+"F16.opExtrude","SWEPT_BODY",BODY,{"disambiguationData":[OSD([sQuery(id+"F9.wireOp",EDGE,"E37.2.0.0"),sQuery(id+"F9.wireOp",EDGE,"E37.2.0.1"),sQuery(id+"F9.wireOp",EDGE,"E37.2.0.2"),sQuery(id+"F9.wireOp",EDGE,"E37.2.0.3")])]});
            var Q5;
            Q5=makeQuery(id+"F16.opExtrude","SWEPT_BODY",BODY,{"disambiguationData":[OSD([sQuery(id+"F9.wireOp",EDGE,"E37.1.0.0"),sQuery(id+"F9.wireOp",EDGE,"E37.1.0.1"),sQuery(id+"F9.wireOp",EDGE,"E37.1.0.2"),sQuery(id+"F9.wireOp",EDGE,"E37.1.0.3")])]});
            var Q6;
            Q6=makeQuery(id+"F16.opExtrude","SWEPT_BODY",BODY,{"disambiguationData":[OSD([sQuery(id+"F9.wireOp",EDGE,"E36.bottom"),sQuery(id+"F9.wireOp",EDGE,"E36.top"),sQuery(id+"F9.wireOp",EDGE,"E36.left"),sQuery(id+"F9.wireOp",EDGE,"E36.right")])]});
            booleanBodies(context, id + "F17", {"operationType" : BooleanOperationType.UNION, "tools" : qUnion([Q0, Q1, Q2, Q3, Q4, Q5, Q6])});
        }
        {
            var Q0;
            Q0=makeQuery(id+"F8.opExtrude","SWEPT_BODY",BODY,{"disambiguationData":[OSD([sQuery(id+"F7.wireOp",EDGE,"E34.bottom"),sQuery(id+"F7.wireOp",EDGE,"E34.top"),sQuery(id+"F7.wireOp",EDGE,"E34.left"),sQuery(id+"F7.wireOp",EDGE,"E34.right")])]});
            transform(context, id + "F18", {"entities" : qUnion([Q0]), "transformType" : TransformType.TRANSLATION_3D, "dx" : 0 * mm, "dy" : -189 * mm, "dz" : 0 * mm, "makeCopy" : true});
        }
        {
            var Q0;
            Q0=makeQuery(id+"F11.opBoolean","MERGE",FACE,{"derivedFrom":[makeQuery(id+"F6.opExtrude","SWEPT_FACE",FACE,{"disambiguationData":[OSD([sQuery(id+"F3.wireOp",EDGE,"E4.top")])]}),makeQuery(id+"F6.opExtrude","SWEPT_FACE",FACE,{"disambiguationData":[OSD([sQuery(id+"F3.wireOp",EDGE,"E5.1.0.1")])]}),makeQuery(id+"F6.opExtrude","SWEPT_FACE",FACE,{"disambiguationData":[OSD([sQuery(id+"F3.wireOp",EDGE,"E5.2.0.1")])]}),makeQuery(id+"F6.opExtrude","SWEPT_FACE",FACE,{"disambiguationData":[OSD([sQuery(id+"F3.wireOp",EDGE,"E5.3.0.1")])]}),makeQuery(id+"F6.opExtrude","SWEPT_FACE",FACE,{"disambiguationData":[OSD([sQuery(id+"F3.wireOp",EDGE,"E5.4.0.1")])]}),makeQuery(id+"F6.opExtrude","SWEPT_FACE",FACE,{"disambiguationData":[OSD([sQuery(id+"F3.wireOp",EDGE,"E5.5.0.1")])]}),makeQuery(id+"F8.opExtrude","SWEPT_FACE",FACE,{"disambiguationData":[OSD([sQuery(id+"F7.wireOp",EDGE,"E34.top")])]})]});
            var sketch = newSketch(context, id + "F19", { "sketchPlane" : qUnion([Q0])});
            skLineSegment(sketch, "E93", {"start": v(-97, 105) * mm, "end": v(-92, 105) * mm});
            skLineSegment(sketch, "E94", {"start": v(-97, 5) * mm, "end": v(-92, 5) * mm});
            skPoint(sketch, "E95", {"position": v(-97, 103.5) * mm});
            skLineSegment(sketch, "E96.bottom", {"start": v(-97, 103.5) * mm, "end": v(-92, 103.5) * mm});
            skLineSegment(sketch, "E96.top", {"start": v(-97, 94.65) * mm, "end": v(-92, 94.65) * mm});
            skLineSegment(sketch, "E96.left", {"start": v(-97, 103.5) * mm, "end": v(-97, 94.65) * mm});
            skLineSegment(sketch, "E96.right", {"start": v(-92, 103.5) * mm, "end": v(-92, 94.65) * mm});
            skLineSegment(sketch, "E97.1.0.0", {"start": v(-97, 77.02) * mm, "end": v(-92, 77.02) * mm});
            skLineSegment(sketch, "E97.1.0.1", {"start": v(-97, 85.87) * mm, "end": v(-97, 77.02) * mm});
            skLineSegment(sketch, "E97.1.0.2", {"start": v(-97, 85.87) * mm, "end": v(-92, 85.87) * mm});
            skLineSegment(sketch, "E97.1.0.3", {"start": v(-92, 85.87) * mm, "end": v(-92, 77.02) * mm});
            skLineSegment(sketch, "E97.2.0.0", {"start": v(-97, 59.4) * mm, "end": v(-92, 59.4) * mm});
            skLineSegment(sketch, "E97.2.0.1", {"start": v(-97, 68.24) * mm, "end": v(-97, 59.4) * mm});
            skLineSegment(sketch, "E97.2.0.2", {"start": v(-97, 68.24) * mm, "end": v(-92, 68.24) * mm});
            skLineSegment(sketch, "E97.2.0.3", {"start": v(-92, 68.24) * mm, "end": v(-92, 59.4) * mm});
            skLineSegment(sketch, "E97.3.0.0", {"start": v(-97, 41.76) * mm, "end": v(-92, 41.76) * mm});
            skLineSegment(sketch, "E97.3.0.1", {"start": v(-97, 50.6) * mm, "end": v(-97, 41.76) * mm});
            skLineSegment(sketch, "E97.3.0.2", {"start": v(-97, 50.6) * mm, "end": v(-92, 50.6) * mm});
            skLineSegment(sketch, "E97.3.0.3", {"start": v(-92, 50.6) * mm, "end": v(-92, 41.76) * mm});
            skLineSegment(sketch, "E97.4.0.0", {"start": v(-97, 24.13) * mm, "end": v(-92, 24.13) * mm});
            skLineSegment(sketch, "E97.4.0.1", {"start": v(-97, 32.98) * mm, "end": v(-97, 24.13) * mm});
            skLineSegment(sketch, "E97.4.0.2", {"start": v(-97, 32.98) * mm, "end": v(-92, 32.98) * mm});
            skLineSegment(sketch, "E97.4.0.3", {"start": v(-92, 32.98) * mm, "end": v(-92, 24.13) * mm});
            skLineSegment(sketch, "E97.5.0.0", {"start": v(-97, 6.5) * mm, "end": v(-92, 6.5) * mm});
            skLineSegment(sketch, "E97.5.0.1", {"start": v(-97, 15.35) * mm, "end": v(-97, 6.5) * mm});
            skLineSegment(sketch, "E97.5.0.2", {"start": v(-97, 15.35) * mm, "end": v(-92, 15.35) * mm});
            skLineSegment(sketch, "E97.5.0.3", {"start": v(-92, 15.35) * mm, "end": v(-92, 6.5) * mm});
            skLineSegment(sketch, "E97.direction1", {"start": v(-97, 94.65) * mm, "end": v(-97, 77.02) * mm, "construction": true});
            skSolve(sketch);
        }
        {
            var Q0;
            Q0=makeQuery(id+"F19.imprint","IMPRINT",FACE,{"disambiguationData":[TD([[makeQuery(id+"F19.imprint","IMPRINT",EDGE,{"derivedFrom":sQuery(id+"F19.wireOp",EDGE,"E96.bottom")}),-1.0]])]});
            var Q1;
            Q1=makeQuery(id+"F19.imprint","IMPRINT",FACE,{"disambiguationData":[TD([[makeQuery(id+"F19.imprint","IMPRINT",EDGE,{"derivedFrom":sQuery(id+"F19.wireOp",EDGE,"E97.1.0.0")}),1.0]])]});
            var Q2;
            Q2=makeQuery(id+"F19.imprint","IMPRINT",FACE,{"disambiguationData":[TD([[makeQuery(id+"F19.imprint","IMPRINT",EDGE,{"derivedFrom":sQuery(id+"F19.wireOp",EDGE,"E97.2.0.0")}),1.0]])]});
            var Q3;
            Q3=makeQuery(id+"F19.imprint","IMPRINT",FACE,{"disambiguationData":[TD([[makeQuery(id+"F19.imprint","IMPRINT",EDGE,{"derivedFrom":sQuery(id+"F19.wireOp",EDGE,"E97.3.0.0")}),1.0]])]});
            var Q4;
            Q4=makeQuery(id+"F19.imprint","IMPRINT",FACE,{"disambiguationData":[TD([[makeQuery(id+"F19.imprint","IMPRINT",EDGE,{"derivedFrom":sQuery(id+"F19.wireOp",EDGE,"E97.4.0.0")}),1.0]])]});
            var Q5;
            Q5=makeQuery(id+"F19.imprint","IMPRINT",FACE,{"disambiguationData":[TD([[makeQuery(id+"F19.imprint","IMPRINT",EDGE,{"derivedFrom":sQuery(id+"F19.wireOp",EDGE,"E97.5.0.0")}),1.0]])]});
            extrude(context, id + "F20", {"entities" : qUnion([Q0, Q1, Q2, Q3, Q4, Q5]), "operationType" : NewBodyOperationType.REMOVE, "oppositeDirection" : true, "depth" : 25 * mm, "offsetDistance" : 25 * mm});
        }
        {
            var Q0;
            Q0=qSketchRegion(id+"F19",true);
            var Q1;
            Q1=makeQuery(id+"F11.opBoolean","MERGE",FACE,{"derivedFrom":[makeQuery(id+"F6.opExtrude","SWEPT_FACE",FACE,{"disambiguationData":[OSD([sQuery(id+"F5.wireOp",EDGE,"E33.0")])]}),makeQuery(id+"F6.opExtrude","SWEPT_FACE",FACE,{"disambiguationData":[OSD([sQuery(id+"F3.wireOp",EDGE,"E5.1.0.2")])]}),makeQuery(id+"F6.opExtrude","SWEPT_FACE",FACE,{"disambiguationData":[OSD([sQuery(id+"F3.wireOp",EDGE,"E5.2.0.2")])]}),makeQuery(id+"F6.opExtrude","SWEPT_FACE",FACE,{"disambiguationData":[OSD([sQuery(id+"F3.wireOp",EDGE,"E5.3.0.2")])]}),makeQuery(id+"F6.opExtrude","SWEPT_FACE",FACE,{"disambiguationData":[OSD([sQuery(id+"F3.wireOp",EDGE,"E5.4.0.2")])]}),makeQuery(id+"F6.opExtrude","SWEPT_FACE",FACE,{"disambiguationData":[OSD([sQuery(id+"F3.wireOp",EDGE,"E5.5.0.2")])]}),makeQuery(id+"F8.opExtrude","SWEPT_FACE",FACE,{"disambiguationData":[OSD([sQuery(id+"F7.wireOp",EDGE,"E34.bottom")])]})]});
            extrude(context, id + "F21", {"entities" : qUnion([Q0]), "endBound" : BoundingType.UP_TO_SURFACE, "oppositeDirection" : true, "depth" : 25 * mm, "endBoundEntityFace" : qUnion([Q1]), "offsetDistance" : 25 * mm});
        }
        {
            var Q0;
            Q0=makeQuery(id+"F15.opExtrude","SWEPT_BODY",BODY,{"disambiguationData":[OSD([sQuery(id+"F14.wireOp",EDGE,"E92.bottom"),sQuery(id+"F14.wireOp",EDGE,"E92.top"),sQuery(id+"F14.wireOp",EDGE,"E92.left"),sQuery(id+"F14.wireOp",EDGE,"E92.right")])]});
            var Q1;
            Q1=makeQuery(id+"F21.opExtrude","SWEPT_BODY",BODY,{"disambiguationData":[OSD([sQuery(id+"F19.wireOp",EDGE,"E96.bottom"),sQuery(id+"F19.wireOp",EDGE,"E96.top"),sQuery(id+"F19.wireOp",EDGE,"E96.left"),sQuery(id+"F19.wireOp",EDGE,"E96.right")])]});
            var Q2;
            Q2=makeQuery(id+"F21.opExtrude","SWEPT_BODY",BODY,{"disambiguationData":[OSD([sQuery(id+"F19.wireOp",EDGE,"E97.1.0.0"),sQuery(id+"F19.wireOp",EDGE,"E97.1.0.1"),sQuery(id+"F19.wireOp",EDGE,"E97.1.0.2"),sQuery(id+"F19.wireOp",EDGE,"E97.1.0.3")])]});
            var Q3;
            Q3=makeQuery(id+"F21.opExtrude","SWEPT_BODY",BODY,{"disambiguationData":[OSD([sQuery(id+"F19.wireOp",EDGE,"E97.2.0.0"),sQuery(id+"F19.wireOp",EDGE,"E97.2.0.1"),sQuery(id+"F19.wireOp",EDGE,"E97.2.0.2"),sQuery(id+"F19.wireOp",EDGE,"E97.2.0.3")])]});
            var Q4;
            Q4=makeQuery(id+"F21.opExtrude","SWEPT_BODY",BODY,{"disambiguationData":[OSD([sQuery(id+"F19.wireOp",EDGE,"E97.3.0.0"),sQuery(id+"F19.wireOp",EDGE,"E97.3.0.1"),sQuery(id+"F19.wireOp",EDGE,"E97.3.0.2"),sQuery(id+"F19.wireOp",EDGE,"E97.3.0.3")])]});
            var Q5;
            Q5=makeQuery(id+"F21.opExtrude","SWEPT_BODY",BODY,{"disambiguationData":[OSD([sQuery(id+"F19.wireOp",EDGE,"E97.4.0.0"),sQuery(id+"F19.wireOp",EDGE,"E97.4.0.1"),sQuery(id+"F19.wireOp",EDGE,"E97.4.0.2"),sQuery(id+"F19.wireOp",EDGE,"E97.4.0.3")])]});
            var Q6;
            Q6=makeQuery(id+"F21.opExtrude","SWEPT_BODY",BODY,{"disambiguationData":[OSD([sQuery(id+"F19.wireOp",EDGE,"E97.5.0.0"),sQuery(id+"F19.wireOp",EDGE,"E97.5.0.1"),sQuery(id+"F19.wireOp",EDGE,"E97.5.0.2"),sQuery(id+"F19.wireOp",EDGE,"E97.5.0.3")])]});
            booleanBodies(context, id + "F22", {"operationType" : BooleanOperationType.UNION, "tools" : qUnion([Q0, Q1, Q2, Q3, Q4, Q5, Q6])});
        }
        {
            var Q0;
            {var subQ35=sQuery(id+"F19.wireOp",EDGE,"E93");Q0=makeQuery(id+"F19.imprint","IMPRINT",FACE,{"disambiguationData":[TD([[makeQuery(id+"F19.imprint","IMPRINT",EDGE,{"derivedFrom":subQ35}),-1.0]])]});}
            var sketch = newSketch(context, id + "F23", { "sketchPlane" : qUnion([Q0])});
            skLineSegment(sketch, "E98.MirrorCS", {"start": v(92, 94.65) * mm, "end": v(92, 103.5) * mm});
            skLineSegment(sketch, "E99.MirrorCS", {"start": v(92, 103.5) * mm, "end": v(97, 103.5) * mm});
            skLineSegment(sketch, "E100.MirrorCS", {"start": v(97, 103.5) * mm, "end": v(97, 94.65) * mm});
            skLineSegment(sketch, "E101.MirrorCS", {"start": v(97, 94.65) * mm, "end": v(92, 94.65) * mm});
            skLineSegment(sketch, "E102.MirrorCS", {"start": v(97, 77.02) * mm, "end": v(92, 77.02) * mm});
            skLineSegment(sketch, "E103.MirrorCS", {"start": v(97, 85.87) * mm, "end": v(97, 77.02) * mm});
            skLineSegment(sketch, "E104.MirrorCS", {"start": v(92, 77.02) * mm, "end": v(92, 85.87) * mm});
            skLineSegment(sketch, "E105.MirrorCS", {"start": v(92, 85.87) * mm, "end": v(97, 85.87) * mm});
            skLineSegment(sketch, "E106.MirrorCS", {"start": v(92, 32.98) * mm, "end": v(97, 32.98) * mm});
            skLineSegment(sketch, "E107.MirrorCS", {"start": v(92, 68.24) * mm, "end": v(97, 68.24) * mm});
            skLineSegment(sketch, "E108.MirrorCS", {"start": v(97, 6.5) * mm, "end": v(92, 6.5) * mm});
            skLineSegment(sketch, "E109.MirrorCS", {"start": v(92, 15.35) * mm, "end": v(97, 15.35) * mm});
            skLineSegment(sketch, "E110.MirrorCS", {"start": v(97, 59.4) * mm, "end": v(92, 59.4) * mm});
            skLineSegment(sketch, "E111.MirrorCS", {"start": v(97, 41.76) * mm, "end": v(92, 41.76) * mm});
            skLineSegment(sketch, "E112.MirrorCS", {"start": v(97, 24.13) * mm, "end": v(92, 24.13) * mm});
            skLineSegment(sketch, "E113.MirrorCS", {"start": v(92, 50.6) * mm, "end": v(97, 50.6) * mm});
            skLineSegment(sketch, "E114.MirrorCS", {"start": v(92, 59.4) * mm, "end": v(92, 68.24) * mm});
            skLineSegment(sketch, "E115.MirrorCS", {"start": v(92, 41.76) * mm, "end": v(92, 50.6) * mm});
            skLineSegment(sketch, "E116.MirrorCS", {"start": v(92, 24.13) * mm, "end": v(92, 32.98) * mm});
            skLineSegment(sketch, "E117.MirrorCS", {"start": v(97, 50.6) * mm, "end": v(97, 41.76) * mm});
            skLineSegment(sketch, "E118.MirrorCS", {"start": v(92, 6.5) * mm, "end": v(92, 15.35) * mm});
            skLineSegment(sketch, "E119.MirrorCS", {"start": v(97, 15.35) * mm, "end": v(97, 6.5) * mm});
            skLineSegment(sketch, "E120.MirrorCS", {"start": v(97, 68.24) * mm, "end": v(97, 59.4) * mm});
            skLineSegment(sketch, "E121.MirrorCS", {"start": v(97, 32.98) * mm, "end": v(97, 24.13) * mm});
            skSolve(sketch);
        }
        {
            var Q0;
            Q0=qSketchRegion(id+"F23",true);
            extrude(context, id + "F24", {"entities" : qUnion([Q0]), "operationType" : NewBodyOperationType.REMOVE, "oppositeDirection" : true, "depth" : 25 * mm, "offsetDistance" : 25 * mm});
        }
        {
            var Q0;
            Q0=makeQuery(id+"F18.opPattern","COPY",FACE,{"derivedFrom":makeQuery(id+"F11.opBoolean","MERGE",FACE,{"derivedFrom":[makeQuery(id+"F6.opExtrude","SWEPT_FACE",FACE,{"disambiguationData":[OSD([sQuery(id+"F5.wireOp",EDGE,"E33.0")])]}),makeQuery(id+"F6.opExtrude","SWEPT_FACE",FACE,{"disambiguationData":[OSD([sQuery(id+"F3.wireOp",EDGE,"E5.1.0.2")])]}),makeQuery(id+"F6.opExtrude","SWEPT_FACE",FACE,{"disambiguationData":[OSD([sQuery(id+"F3.wireOp",EDGE,"E5.2.0.2")])]}),makeQuery(id+"F6.opExtrude","SWEPT_FACE",FACE,{"disambiguationData":[OSD([sQuery(id+"F3.wireOp",EDGE,"E5.3.0.2")])]}),makeQuery(id+"F6.opExtrude","SWEPT_FACE",FACE,{"disambiguationData":[OSD([sQuery(id+"F3.wireOp",EDGE,"E5.4.0.2")])]}),makeQuery(id+"F6.opExtrude","SWEPT_FACE",FACE,{"disambiguationData":[OSD([sQuery(id+"F3.wireOp",EDGE,"E5.5.0.2")])]}),makeQuery(id+"F8.opExtrude","SWEPT_FACE",FACE,{"disambiguationData":[OSD([sQuery(id+"F7.wireOp",EDGE,"E34.bottom")])]})]}),"instanceName":"1"});
            var sketch = newSketch(context, id + "F25", { "sketchPlane" : qUnion([Q0])});
            skLineSegment(sketch, "E122.0", {"start": v(97, 105) * mm, "end": v(92, 105) * mm});
            skLineSegment(sketch, "E123", {"start": v(97, 5) * mm, "end": v(92, 5) * mm});
            skPoint(sketch, "E124", {"position": v(91.95, 103.5) * mm});
            skLineSegment(sketch, "E125.bottom", {"start": v(91.95, 103.5) * mm, "end": v(96.95, 103.5) * mm});
            skLineSegment(sketch, "E125.top", {"start": v(91.95, 94.66) * mm, "end": v(96.95, 94.66) * mm});
            skLineSegment(sketch, "E125.left", {"start": v(91.95, 103.5) * mm, "end": v(91.95, 94.66) * mm});
            skLineSegment(sketch, "E125.right", {"start": v(96.95, 103.5) * mm, "end": v(96.95, 94.66) * mm});
            skLineSegment(sketch, "E126.1.0.0", {"start": v(91.95, 85.87) * mm, "end": v(96.95, 85.87) * mm});
            skLineSegment(sketch, "E126.1.0.1", {"start": v(96.95, 85.87) * mm, "end": v(96.95, 77.02) * mm});
            skLineSegment(sketch, "E126.1.0.2", {"start": v(91.95, 85.87) * mm, "end": v(91.95, 77.02) * mm});
            skLineSegment(sketch, "E126.1.0.3", {"start": v(91.95, 77.02) * mm, "end": v(96.95, 77.02) * mm});
            skLineSegment(sketch, "E126.2.0.0", {"start": v(91.95, 68.24) * mm, "end": v(96.95, 68.24) * mm});
            skLineSegment(sketch, "E126.2.0.1", {"start": v(96.95, 68.24) * mm, "end": v(96.95, 59.4) * mm});
            skLineSegment(sketch, "E126.2.0.2", {"start": v(91.95, 68.24) * mm, "end": v(91.95, 59.4) * mm});
            skLineSegment(sketch, "E126.2.0.3", {"start": v(91.95, 59.4) * mm, "end": v(96.95, 59.4) * mm});
            skLineSegment(sketch, "E126.3.0.0", {"start": v(91.95, 50.6) * mm, "end": v(96.95, 50.6) * mm});
            skLineSegment(sketch, "E126.3.0.1", {"start": v(96.95, 50.6) * mm, "end": v(96.95, 41.76) * mm});
            skLineSegment(sketch, "E126.3.0.2", {"start": v(91.95, 50.6) * mm, "end": v(91.95, 41.76) * mm});
            skLineSegment(sketch, "E126.3.0.3", {"start": v(91.95, 41.76) * mm, "end": v(96.95, 41.76) * mm});
            skLineSegment(sketch, "E126.4.0.0", {"start": v(91.95, 32.98) * mm, "end": v(96.95, 32.98) * mm});
            skLineSegment(sketch, "E126.4.0.1", {"start": v(96.95, 32.98) * mm, "end": v(96.95, 24.13) * mm});
            skLineSegment(sketch, "E126.4.0.2", {"start": v(91.95, 32.98) * mm, "end": v(91.95, 24.13) * mm});
            skLineSegment(sketch, "E126.4.0.3", {"start": v(91.95, 24.13) * mm, "end": v(96.95, 24.13) * mm});
            skLineSegment(sketch, "E126.5.0.0", {"start": v(91.95, 15.35) * mm, "end": v(96.95, 15.35) * mm});
            skLineSegment(sketch, "E126.5.0.1", {"start": v(96.95, 15.35) * mm, "end": v(96.95, 6.5) * mm});
            skLineSegment(sketch, "E126.5.0.2", {"start": v(91.95, 15.35) * mm, "end": v(91.95, 6.5) * mm});
            skLineSegment(sketch, "E126.5.0.3", {"start": v(91.95, 6.5) * mm, "end": v(96.95, 6.5) * mm});
            skLineSegment(sketch, "E126.direction1", {"start": v(91.95, 103.5) * mm, "end": v(91.95, 85.87) * mm, "construction": true});
            skSolve(sketch);
        }
        {
            var Q0;
            Q0=makeQuery(id+"F25.imprint","IMPRINT",FACE,{"disambiguationData":[TD([[makeQuery(id+"F25.imprint","IMPRINT",EDGE,{"derivedFrom":sQuery(id+"F25.wireOp",EDGE,"E125.bottom")}),-1.0]])]});
            var Q1;
            Q1=makeQuery(id+"F25.imprint","IMPRINT",FACE,{"disambiguationData":[TD([[makeQuery(id+"F25.imprint","IMPRINT",EDGE,{"derivedFrom":sQuery(id+"F25.wireOp",EDGE,"E126.1.0.0")}),-1.0]])]});
            var Q2;
            Q2=makeQuery(id+"F25.imprint","IMPRINT",FACE,{"disambiguationData":[TD([[makeQuery(id+"F25.imprint","IMPRINT",EDGE,{"derivedFrom":sQuery(id+"F25.wireOp",EDGE,"E126.2.0.0")}),-1.0]])]});
            var Q3;
            Q3=makeQuery(id+"F25.imprint","IMPRINT",FACE,{"disambiguationData":[TD([[makeQuery(id+"F25.imprint","IMPRINT",EDGE,{"derivedFrom":sQuery(id+"F25.wireOp",EDGE,"E126.3.0.0")}),-1.0]])]});
            var Q4;
            Q4=makeQuery(id+"F25.imprint","IMPRINT",FACE,{"disambiguationData":[TD([[makeQuery(id+"F25.imprint","IMPRINT",EDGE,{"derivedFrom":sQuery(id+"F25.wireOp",EDGE,"E126.4.0.0")}),-1.0]])]});
            var Q5;
            Q5=makeQuery(id+"F25.imprint","IMPRINT",FACE,{"disambiguationData":[TD([[makeQuery(id+"F25.imprint","IMPRINT",EDGE,{"derivedFrom":sQuery(id+"F25.wireOp",EDGE,"E126.5.0.0")}),-1.0]])]});
            extrude(context, id + "F26", {"entities" : qUnion([Q0, Q1, Q2, Q3, Q4, Q5]), "operationType" : NewBodyOperationType.REMOVE, "oppositeDirection" : true, "depth" : 25 * mm, "offsetDistance" : 25 * mm});
        }
        {
            var Q0;
            Q0=makeQuery(id+"F25.imprint","IMPRINT",FACE,{"disambiguationData":[TD([[makeQuery(id+"F25.imprint","IMPRINT",EDGE,{"derivedFrom":sQuery(id+"F25.wireOp",EDGE,"E125.bottom")}),-1.0]])]});
            var Q1;
            Q1=makeQuery(id+"F25.imprint","IMPRINT",FACE,{"disambiguationData":[TD([[makeQuery(id+"F25.imprint","IMPRINT",EDGE,{"derivedFrom":sQuery(id+"F25.wireOp",EDGE,"E126.1.0.0")}),-1.0]])]});
            var Q2;
            Q2=makeQuery(id+"F25.imprint","IMPRINT",FACE,{"disambiguationData":[TD([[makeQuery(id+"F25.imprint","IMPRINT",EDGE,{"derivedFrom":sQuery(id+"F25.wireOp",EDGE,"E126.2.0.0")}),-1.0]])]});
            var Q3;
            Q3=makeQuery(id+"F25.imprint","IMPRINT",FACE,{"disambiguationData":[TD([[makeQuery(id+"F25.imprint","IMPRINT",EDGE,{"derivedFrom":sQuery(id+"F25.wireOp",EDGE,"E126.3.0.0")}),-1.0]])]});
            var Q4;
            Q4=makeQuery(id+"F25.imprint","IMPRINT",FACE,{"disambiguationData":[TD([[makeQuery(id+"F25.imprint","IMPRINT",EDGE,{"derivedFrom":sQuery(id+"F25.wireOp",EDGE,"E126.4.0.0")}),-1.0]])]});
            var Q5;
            Q5=makeQuery(id+"F25.imprint","IMPRINT",FACE,{"disambiguationData":[TD([[makeQuery(id+"F25.imprint","IMPRINT",EDGE,{"derivedFrom":sQuery(id+"F25.wireOp",EDGE,"E126.5.0.0")}),-1.0]])]});
            var Q6;
            Q6=makeQuery(id+"F18.opPattern","COPY",FACE,{"derivedFrom":makeQuery(id+"F11.opBoolean","MERGE",FACE,{"derivedFrom":[makeQuery(id+"F6.opExtrude","SWEPT_FACE",FACE,{"disambiguationData":[OSD([sQuery(id+"F3.wireOp",EDGE,"E4.top")])]}),makeQuery(id+"F6.opExtrude","SWEPT_FACE",FACE,{"disambiguationData":[OSD([sQuery(id+"F3.wireOp",EDGE,"E5.1.0.1")])]}),makeQuery(id+"F6.opExtrude","SWEPT_FACE",FACE,{"disambiguationData":[OSD([sQuery(id+"F3.wireOp",EDGE,"E5.2.0.1")])]}),makeQuery(id+"F6.opExtrude","SWEPT_FACE",FACE,{"disambiguationData":[OSD([sQuery(id+"F3.wireOp",EDGE,"E5.3.0.1")])]}),makeQuery(id+"F6.opExtrude","SWEPT_FACE",FACE,{"disambiguationData":[OSD([sQuery(id+"F3.wireOp",EDGE,"E5.4.0.1")])]}),makeQuery(id+"F6.opExtrude","SWEPT_FACE",FACE,{"disambiguationData":[OSD([sQuery(id+"F3.wireOp",EDGE,"E5.5.0.1")])]}),makeQuery(id+"F8.opExtrude","SWEPT_FACE",FACE,{"disambiguationData":[OSD([sQuery(id+"F7.wireOp",EDGE,"E34.top")])]})]}),"instanceName":"1"});
            extrude(context, id + "F27", {"entities" : qUnion([Q0, Q1, Q2, Q3, Q4, Q5]), "endBound" : BoundingType.UP_TO_SURFACE, "oppositeDirection" : true, "depth" : 25 * mm, "endBoundEntityFace" : qUnion([Q6]), "offsetDistance" : 25 * mm});
        }
        {
            var Q0;
            Q0=makeQuery(id+"F2.opExtrude","CAP_FACE",FACE,{"disambiguationData":[OSD([sQuery(id+"F1.wireOp",EDGE,"E0.bottom"),sQuery(id+"F1.wireOp",EDGE,"E0.top"),sQuery(id+"F1.wireOp",EDGE,"E0.left"),sQuery(id+"F1.wireOp",EDGE,"E0.right")])],"isStart":false});
            var sketch = newSketch(context, id + "F28", { "sketchPlane" : qUnion([Q0])});
            skLineSegment(sketch, "E127.bottom", {"start": v(-37.62, -42.22) * mm, "end": v(-71.5, -42.22) * mm});
            skLineSegment(sketch, "E127.top", {"start": v(-37.62, 42.22) * mm, "end": v(-71.5, 42.22) * mm});
            skLineSegment(sketch, "E127.left", {"start": v(-37.62, -42.22) * mm, "end": v(-37.62, 42.22) * mm});
            skLineSegment(sketch, "E127.right", {"start": v(-71.5, -42.22) * mm, "end": v(-71.5, 42.22) * mm});
            skPoint(sketch, "E127.middle", {"position": v(-54.56, 0) * mm});
            skLineSegment(sketch, "E128.MirrorCS", {"start": v(37.62, -42.22) * mm, "end": v(37.62, 42.22) * mm});
            skLineSegment(sketch, "E129.MirrorCS", {"start": v(37.62, 42.22) * mm, "end": v(71.5, 42.22) * mm});
            skLineSegment(sketch, "E130.MirrorCS", {"start": v(71.5, -42.22) * mm, "end": v(71.5, 42.22) * mm});
            skLineSegment(sketch, "E131.MirrorCS", {"start": v(37.62, -42.22) * mm, "end": v(71.5, -42.22) * mm});
            skSolve(sketch);
        }
        {
            var Q0;
            Q0=makeQuery(id+"F28.imprint","IMPRINT",FACE,{"disambiguationData":[TD([[makeQuery(id+"F28.imprint","IMPRINT",EDGE,{"derivedFrom":sQuery(id+"F28.wireOp",EDGE,"E127.bottom")}),-1.0]])]});
            var Q1;
            Q1=makeQuery(id+"F28.imprint","IMPRINT",FACE,{"disambiguationData":[TD([[makeQuery(id+"F28.imprint","IMPRINT",EDGE,{"derivedFrom":sQuery(id+"F28.wireOp",EDGE,"E129.MirrorCS")}),-1.0]])]});
            extrude(context, id + "F29", {"entities" : qUnion([Q0, Q1]), "operationType" : NewBodyOperationType.REMOVE, "oppositeDirection" : true, "depth" : 25 * mm, "offsetDistance" : 25 * mm});
        }
    });
